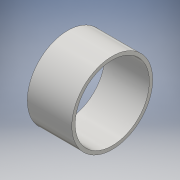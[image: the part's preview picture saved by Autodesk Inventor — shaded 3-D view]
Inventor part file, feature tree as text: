
AUTODESK INVENTOR PART (.ipt)
format: ipt  version: 2016 (Build 200138000, 138)  size: 123,904 bytes
history: native  units: mm
features: extrude x1, sketch x1
ambient origin geometry x8: Origin, YZ Plane, XZ Plane, XY Plane, X Axis, Y Axis, Z Axis, Center Point
bodies: Solid1 (feature_tree)
feature tree (2):
  extrude  "Extrusion1"  Depth=13.2mm
  sketch  "Sketch1"  dims[d0=24.0mm d1=22.0mm d2=13.2mm d3=0.0mm]
